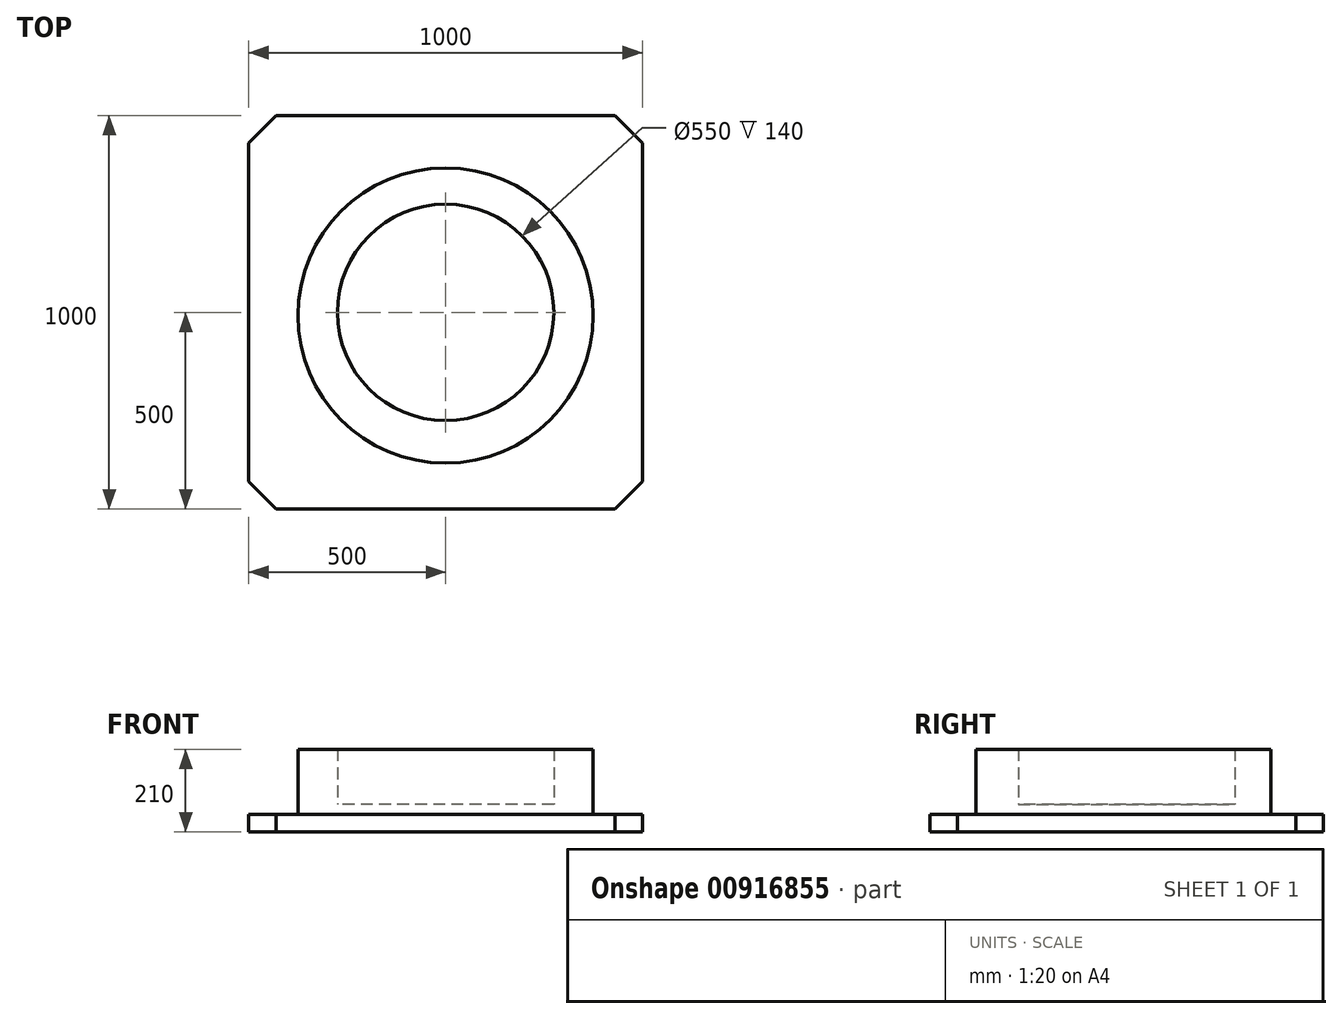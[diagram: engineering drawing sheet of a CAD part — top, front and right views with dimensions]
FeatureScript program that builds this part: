
annotation { "Feature Type Name" : "Feature", "Feature Type Description" : "" }
export const myFeature = defineFeature(function(context is Context, id is Id, definition is map)
    precondition{}
    {
        {
            var Q0;
            Q0=qCreatedBy(makeId("Top.planeOp"),FACE);
            var sketch = newSketch(context, id + "F0", { "sketchPlane" : qUnion([Q0])});
            skLineSegment(sketch, "E0.bottom", {"start": v(430, 500) * mm, "end": v(-430, 500) * mm});
            skLineSegment(sketch, "E0.top", {"start": v(430, -500) * mm, "end": v(-430, -500) * mm});
            skLineSegment(sketch, "E0.left", {"start": v(500, 430) * mm, "end": v(500, -430) * mm});
            skLineSegment(sketch, "E0.right", {"start": v(-500, 430) * mm, "end": v(-500, -430) * mm});
            skPoint(sketch, "E0.middle", {"position": v(0, 0) * mm});
            skLineSegment(sketch, "E1", {"start": v(-500, 430) * mm, "end": v(-430, 500) * mm});
            skLineSegment(sketch, "E2", {"start": v(430, 500) * mm, "end": v(500, 430) * mm});
            skLineSegment(sketch, "E3", {"start": v(-500, -430) * mm, "end": v(-430, -500) * mm});
            skLineSegment(sketch, "E4", {"start": v(430, -500) * mm, "end": v(500, -430) * mm});
            skPoint(sketch, "E5.orphan", {"position": v(-500, 500) * mm});
            skPoint(sketch, "E6.orphan", {"position": v(500, 500) * mm});
            skPoint(sketch, "E7.orphan", {"position": v(500, -500) * mm});
            skPoint(sketch, "E8.orphan", {"position": v(-500, -500) * mm});
            skSolve(sketch);
        }
        {
            var Q0;
            Q0=qSketchRegion(id+"F0",true);
            extrude(context, id + "F1", {"entities" : qUnion([Q0]), "depth" : 45 * mm, "offsetDistance" : 25 * mm});
        }
        {
            var Q0;
            Q0=makeQuery(id+"F1.opExtrude","CAP_FACE",FACE,{"disambiguationData":[OSD([sQuery(id+"F0.wireOp",EDGE,"E0.bottom"),sQuery(id+"F0.wireOp",EDGE,"E0.top"),sQuery(id+"F0.wireOp",EDGE,"E0.left"),sQuery(id+"F0.wireOp",EDGE,"E0.right"),sQuery(id+"F0.wireOp",EDGE,"E1"),sQuery(id+"F0.wireOp",EDGE,"E2"),sQuery(id+"F0.wireOp",EDGE,"E3"),sQuery(id+"F0.wireOp",EDGE,"E4")])],"isStart":false});
            var sketch = newSketch(context, id + "F2", { "sketchPlane" : qUnion([Q0])});
            skCircle(sketch, "E9", {"center": v(0, -8.12) * mm, "radius": 375 * mm});
            skSolve(sketch);
        }
        {
            var Q0;
            Q0=makeQuery(id+"F2.imprint","IMPRINT",FACE,{"disambiguationData":[TD([[makeQuery(id+"F2.imprint","IMPRINT",EDGE,{"derivedFrom":sQuery(id+"F2.wireOp",EDGE,"E9")}),1.0]])]});
            extrude(context, id + "F3", {"entities" : qUnion([Q0]), "operationType" : NewBodyOperationType.ADD, "depth" : 25 * mm, "offsetDistance" : 25 * mm});
        }
        {
            var Q0;
            Q0=makeQuery(id+"F3.opExtrude","CAP_FACE",FACE,{"disambiguationData":[OSD([sQuery(id+"F2.wireOp",EDGE,"E9")])],"isStart":false});
            var sketch = newSketch(context, id + "F4", { "sketchPlane" : qUnion([Q0])});
            skCircle(sketch, "E10", {"center": v(0, 0) * mm, "radius": 275 * mm});
            skSolve(sketch);
        }
        {
            var Q0;
            Q0=makeQuery(id+"F4.imprint","IMPRINT",FACE,{"disambiguationData":[TD([[makeQuery(id+"F4.imprint","IMPRINT",EDGE,{"derivedFrom":sQuery(id+"F4.wireOp",EDGE,"E10")}),-1.0]])]});
            extrude(context, id + "F5", {"entities" : qUnion([Q0]), "operationType" : NewBodyOperationType.ADD, "depth" : 140 * mm, "offsetDistance" : 25 * mm});
        }
    });
